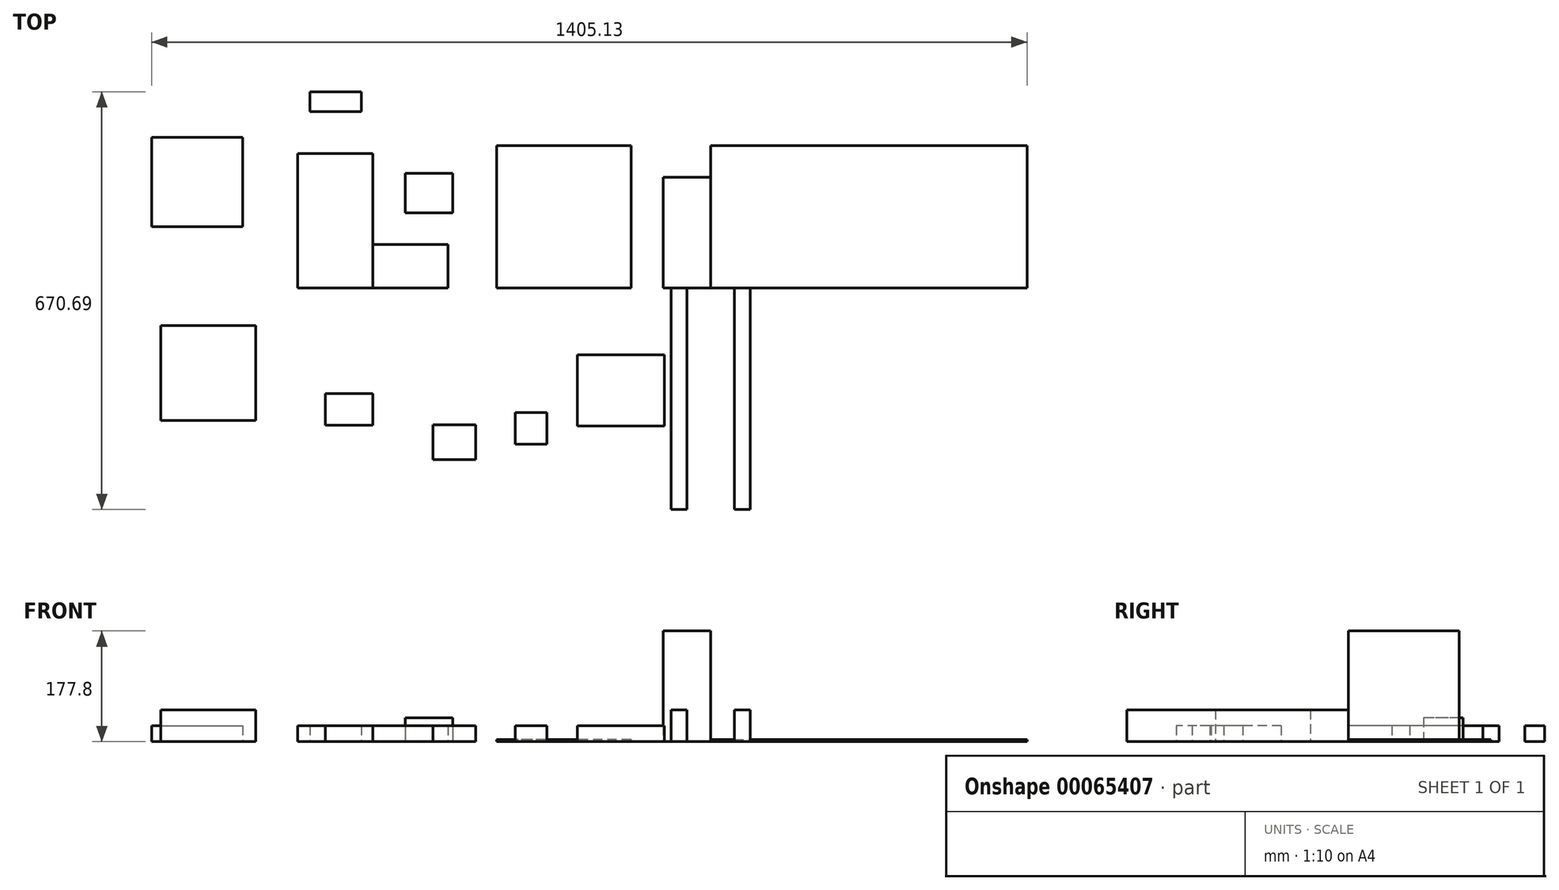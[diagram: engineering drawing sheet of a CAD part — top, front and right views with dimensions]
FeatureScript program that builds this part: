
annotation { "Feature Type Name" : "Feature", "Feature Type Description" : "" }
export const myFeature = defineFeature(function(context is Context, id is Id, definition is map)
    precondition{}
    {
        {
            var Q0;
            Q0=qCreatedBy(makeId("Front.planeOp"),FACE);
            var sketch = newSketch(context, id + "F0", { "sketchPlane" : qUnion([Q0])});
            skLineSegment(sketch, "E0.bottom", {"start": v(-63.5, 50.8) * mm, "end": v(-38.1, 50.8) * mm});
            skLineSegment(sketch, "E0.top", {"start": v(-63.5, 0) * mm, "end": v(-38.1, 0) * mm});
            skLineSegment(sketch, "E0.left", {"start": v(-63.5, 50.8) * mm, "end": v(-63.5, 0) * mm});
            skLineSegment(sketch, "E0.right", {"start": v(-38.1, 50.8) * mm, "end": v(-38.1, 0) * mm});
            skLineSegment(sketch, "E1", {"start": v(0, 0) * mm, "end": v(0, 99.13) * mm, "construction": true});
            skLineSegment(sketch, "E2.MirrorCS", {"start": v(38.1, 50.8) * mm, "end": v(38.1, 0) * mm});
            skLineSegment(sketch, "E3.MirrorCS", {"start": v(63.5, 50.8) * mm, "end": v(63.5, 0) * mm});
            skLineSegment(sketch, "E4.MirrorCS", {"start": v(63.5, 0) * mm, "end": v(38.1, 0) * mm});
            skLineSegment(sketch, "E5.MirrorCS", {"start": v(63.5, 50.8) * mm, "end": v(38.1, 50.8) * mm});
            skLineSegment(sketch, "E6", {"start": v(0, -0.38) * mm, "end": v(-38.1, -0.38) * mm, "construction": true});
            skLineSegment(sketch, "E7", {"start": v(0, 0) * mm, "end": v(76.49, 0) * mm, "construction": true});
            skSolve(sketch);
        }
        {
            var Q0;
            Q0 = qSketchRegion(id + "F0", true);
            extrude(context, id + "F1", {"entities" : qUnion([Q0]), "depth" : 355.6 * mm});
        }
        {
            var Q0;
            Q0=qCreatedBy(makeId("Top.planeOp"),FACE);
            var sketch = newSketch(context, id + "F2", { "sketchPlane" : qUnion([Q0])});
            skLineSegment(sketch, "E8.bottom", {"start": v(0, 0) * mm, "end": v(508, 0) * mm});
            skLineSegment(sketch, "E8.top", {"start": v(0, 228.6) * mm, "end": v(508, 228.6) * mm});
            skLineSegment(sketch, "E8.left", {"start": v(0, 0) * mm, "end": v(0, 228.6) * mm});
            skLineSegment(sketch, "E8.right", {"start": v(508, 0) * mm, "end": v(508, 228.6) * mm});
            skLineSegment(sketch, "E9.bottom", {"start": v(-127.72, 0) * mm, "end": v(-343.62, 0) * mm});
            skLineSegment(sketch, "E9.top", {"start": v(-127.72, 228.6) * mm, "end": v(-343.62, 228.6) * mm});
            skLineSegment(sketch, "E9.left", {"start": v(-127.72, 0) * mm, "end": v(-127.72, 228.6) * mm});
            skLineSegment(sketch, "E9.right", {"start": v(-343.62, 0) * mm, "end": v(-343.62, 228.6) * mm});
            skLineSegment(sketch, "E10.bottom", {"start": v(-542.44, 69.85) * mm, "end": v(-421.8, 69.85) * mm});
            skLineSegment(sketch, "E10.top", {"start": v(-542.44, 0) * mm, "end": v(-421.8, 0) * mm});
            skLineSegment(sketch, "E10.left", {"start": v(-542.44, 69.85) * mm, "end": v(-542.44, 0) * mm});
            skLineSegment(sketch, "E10.right", {"start": v(-421.8, 69.85) * mm, "end": v(-421.8, 0) * mm});
            skLineSegment(sketch, "E11.bottom", {"start": v(-490.2, 184) * mm, "end": v(-414, 184) * mm});
            skLineSegment(sketch, "E11.top", {"start": v(-490.2, 120.5) * mm, "end": v(-414, 120.5) * mm});
            skLineSegment(sketch, "E11.left", {"start": v(-490.2, 184) * mm, "end": v(-490.2, 120.5) * mm});
            skLineSegment(sketch, "E11.right", {"start": v(-414, 184) * mm, "end": v(-414, 120.5) * mm});
            skLineSegment(sketch, "E12.bottom", {"start": v(-897.13, 241.82) * mm, "end": v(-751.08, 241.82) * mm});
            skLineSegment(sketch, "E12.top", {"start": v(-897.13, 98.57) * mm, "end": v(-751.08, 98.57) * mm});
            skLineSegment(sketch, "E12.left", {"start": v(-897.13, 241.82) * mm, "end": v(-897.13, 98.57) * mm});
            skLineSegment(sketch, "E12.right", {"start": v(-751.08, 241.82) * mm, "end": v(-751.08, 98.57) * mm});
            skLineSegment(sketch, "E13.bottom", {"start": v(-642.93, 315.1) * mm, "end": v(-560.38, 315.1) * mm});
            skLineSegment(sketch, "E13.top", {"start": v(-642.93, 283.34) * mm, "end": v(-560.38, 283.34) * mm});
            skLineSegment(sketch, "E13.left", {"start": v(-642.93, 315.1) * mm, "end": v(-642.93, 283.34) * mm});
            skLineSegment(sketch, "E13.right", {"start": v(-560.38, 315.1) * mm, "end": v(-560.38, 283.34) * mm});
            skLineSegment(sketch, "E14.bottom", {"start": v(-663.1, 215.9) * mm, "end": v(-542.44, 215.9) * mm});
            skLineSegment(sketch, "E14.top", {"start": v(-663.1, 0) * mm, "end": v(-542.44, 0) * mm});
            skLineSegment(sketch, "E14.left", {"start": v(-663.1, 215.9) * mm, "end": v(-663.1, 0) * mm});
            skLineSegment(sketch, "E14.right", {"start": v(-542.44, 215.9) * mm, "end": v(-542.44, 0) * mm});
            skLineSegment(sketch, "E15.bottom", {"start": v(-313.3, -199.68) * mm, "end": v(-262.5, -199.68) * mm});
            skLineSegment(sketch, "E15.top", {"start": v(-313.3, -250.48) * mm, "end": v(-262.5, -250.48) * mm});
            skLineSegment(sketch, "E15.left", {"start": v(-313.3, -199.68) * mm, "end": v(-313.3, -250.48) * mm});
            skLineSegment(sketch, "E15.right", {"start": v(-262.5, -199.68) * mm, "end": v(-262.5, -250.48) * mm});
            skLineSegment(sketch, "E16.bottom", {"start": v(-445.68, -219.92) * mm, "end": v(-377.1, -219.92) * mm});
            skLineSegment(sketch, "E16.top", {"start": v(-445.68, -275.8) * mm, "end": v(-377.1, -275.8) * mm});
            skLineSegment(sketch, "E16.left", {"start": v(-445.68, -219.92) * mm, "end": v(-445.68, -275.8) * mm});
            skLineSegment(sketch, "E16.right", {"start": v(-377.1, -219.92) * mm, "end": v(-377.1, -275.8) * mm});
            skLineSegment(sketch, "E17.bottom", {"start": v(-618.64, -169.46) * mm, "end": v(-542.44, -169.46) * mm});
            skLineSegment(sketch, "E17.top", {"start": v(-618.64, -220.26) * mm, "end": v(-542.44, -220.26) * mm});
            skLineSegment(sketch, "E17.left", {"start": v(-618.64, -169.46) * mm, "end": v(-618.64, -220.26) * mm});
            skLineSegment(sketch, "E17.right", {"start": v(-542.44, -169.46) * mm, "end": v(-542.44, -220.26) * mm});
            skLineSegment(sketch, "E18.bottom", {"start": v(-882.38, -60.5) * mm, "end": v(-729.98, -60.5) * mm});
            skLineSegment(sketch, "E18.top", {"start": v(-882.38, -212.9) * mm, "end": v(-729.98, -212.9) * mm});
            skLineSegment(sketch, "E18.left", {"start": v(-882.38, -60.5) * mm, "end": v(-882.38, -212.9) * mm});
            skLineSegment(sketch, "E18.right", {"start": v(-729.98, -60.5) * mm, "end": v(-729.98, -212.9) * mm});
            skLineSegment(sketch, "E19.bottom", {"start": v(-213.58, -107.5) * mm, "end": v(-73.88, -107.5) * mm});
            skLineSegment(sketch, "E19.top", {"start": v(-213.58, -221.8) * mm, "end": v(-73.88, -221.8) * mm});
            skLineSegment(sketch, "E19.left", {"start": v(-213.58, -107.5) * mm, "end": v(-213.58, -221.8) * mm});
            skLineSegment(sketch, "E19.right", {"start": v(-73.88, -107.5) * mm, "end": v(-73.88, -221.8) * mm});
            skSolve(sketch);
        }
        {
            var Q0;
            Q0=makeQuery(id+"F2.imprint","IMPRINT",FACE,{"disambiguationData":[TD([[makeQuery(id+"F2.imprint","IMPRINT",EDGE,{"derivedFrom":sQuery(id+"F2.wireOp",EDGE,"E8.bottom")}),1.0]])]});
            var Q1;
            Q1=makeQuery(id+"F2.imprint","IMPRINT",FACE,{"disambiguationData":[TD([[makeQuery(id+"F2.imprint","IMPRINT",EDGE,{"derivedFrom":sQuery(id+"F2.wireOp",EDGE,"E9.bottom")}),-1.0]])]});
            extrude(context, id + "F3", {"entities" : qUnion([Q0, Q1]), "depth" : 3.17 * mm});
        }
        {
            var Q0;
            Q0=qCreatedBy(makeId("Top.planeOp"),FACE);
            var sketch = newSketch(context, id + "F4", { "sketchPlane" : qUnion([Q0])});
            skLineSegment(sketch, "E20.bottom", {"start": v(-76.2, 177.8) * mm, "end": v(0, 177.8) * mm});
            skLineSegment(sketch, "E20.top", {"start": v(-76.2, 0) * mm, "end": v(0, 0) * mm});
            skLineSegment(sketch, "E20.left", {"start": v(-76.2, 177.8) * mm, "end": v(-76.2, 0) * mm});
            skLineSegment(sketch, "E20.right", {"start": v(0, 177.8) * mm, "end": v(0, 0) * mm});
            skSolve(sketch);
        }
        {
            var Q0;
            Q0=makeQuery(id+"F4.imprint","IMPRINT",FACE,{"disambiguationData":[TD([[makeQuery(id+"F4.imprint","IMPRINT",EDGE,{"derivedFrom":sQuery(id+"F4.wireOp",EDGE,"E20.bottom")}),-1.0]])]});
            extrude(context, id + "F5", {"entities" : qUnion([Q0]), "depth" : 177.8 * mm});
        }
        {
            var Q0;
            Q0=makeQuery(id+"F2.imprint","IMPRINT",FACE,{"disambiguationData":[TD([[makeQuery(id+"F2.imprint","IMPRINT",EDGE,{"derivedFrom":sQuery(id+"F2.wireOp",EDGE,"E10.bottom")}),-1.0]])]});
            extrude(context, id + "F6", {"entities" : qUnion([Q0]), "depth" : 25.4 * mm});
        }
        {
            var Q0;
            Q0=makeQuery(id+"F2.imprint","IMPRINT",FACE,{"disambiguationData":[TD([[makeQuery(id+"F2.imprint","IMPRINT",EDGE,{"derivedFrom":sQuery(id+"F2.wireOp",EDGE,"E11.bottom")}),-1.0]])]});
            extrude(context, id + "F7", {"entities" : qUnion([Q0]), "depth" : 38.1 * mm});
        }
        {
            var Q0;
            Q0=makeQuery(id+"F2.imprint","IMPRINT",FACE,{"disambiguationData":[TD([[makeQuery(id+"F2.imprint","IMPRINT",EDGE,{"derivedFrom":sQuery(id+"F2.wireOp",EDGE,"E12.bottom")}),-1.0]])]});
            extrude(context, id + "F8", {"entities" : qUnion([Q0]), "depth" : 25.4 * mm});
        }
        {
            var Q0;
            Q0=makeQuery(id+"F2.imprint","IMPRINT",FACE,{"disambiguationData":[TD([[makeQuery(id+"F2.imprint","IMPRINT",EDGE,{"derivedFrom":sQuery(id+"F2.wireOp",EDGE,"E13.bottom")}),-1.0]])]});
            extrude(context, id + "F9", {"entities" : qUnion([Q0]), "depth" : 25.4 * mm});
        }
        {
            var Q0;
            {var subQ2=sQuery(id+"F2.wireOp",EDGE,"E14.bottom");Q0=makeQuery(id+"F2.imprint","IMPRINT",FACE,{"disambiguationData":[TD([[makeQuery(id+"F2.imprint","IMPRINT",EDGE,{"derivedFrom":subQ2}),-1.0]])]});}
            extrude(context, id + "F10", {"entities" : qUnion([Q0]), "depth" : 25.4 * mm});
        }
        {
            var Q0;
            Q0=makeQuery(id+"F2.imprint","IMPRINT",FACE,{"disambiguationData":[TD([[makeQuery(id+"F2.imprint","IMPRINT",EDGE,{"derivedFrom":sQuery(id+"F2.wireOp",EDGE,"E15.bottom")}),-1.0]])]});
            extrude(context, id + "F11", {"entities" : qUnion([Q0]), "depth" : 25.4 * mm});
        }
        {
            var Q0;
            Q0=makeQuery(id+"F2.imprint","IMPRINT",FACE,{"disambiguationData":[TD([[makeQuery(id+"F2.imprint","IMPRINT",EDGE,{"derivedFrom":sQuery(id+"F2.wireOp",EDGE,"E16.bottom")}),-1.0]])]});
            extrude(context, id + "F12", {"entities" : qUnion([Q0]), "depth" : 25.4 * mm});
        }
        {
            var Q0;
            Q0=makeQuery(id+"F2.imprint","IMPRINT",FACE,{"disambiguationData":[TD([[makeQuery(id+"F2.imprint","IMPRINT",EDGE,{"derivedFrom":sQuery(id+"F2.wireOp",EDGE,"E17.bottom")}),-1.0]])]});
            extrude(context, id + "F13", {"entities" : qUnion([Q0]), "depth" : 25.4 * mm});
        }
        {
            var Q0;
            Q0=makeQuery(id+"F2.imprint","IMPRINT",FACE,{"disambiguationData":[TD([[makeQuery(id+"F2.imprint","IMPRINT",EDGE,{"derivedFrom":sQuery(id+"F2.wireOp",EDGE,"E18.bottom")}),-1.0]])]});
            extrude(context, id + "F14", {"entities" : qUnion([Q0]), "depth" : 50.8 * mm});
        }
        {
            var Q0;
            Q0=makeQuery(id+"F2.imprint","IMPRINT",FACE,{"disambiguationData":[TD([[makeQuery(id+"F2.imprint","IMPRINT",EDGE,{"derivedFrom":sQuery(id+"F2.wireOp",EDGE,"E19.bottom")}),-1.0]])]});
            extrude(context, id + "F15", {"entities" : qUnion([Q0]), "depth" : 25.4 * mm});
        }
    });
